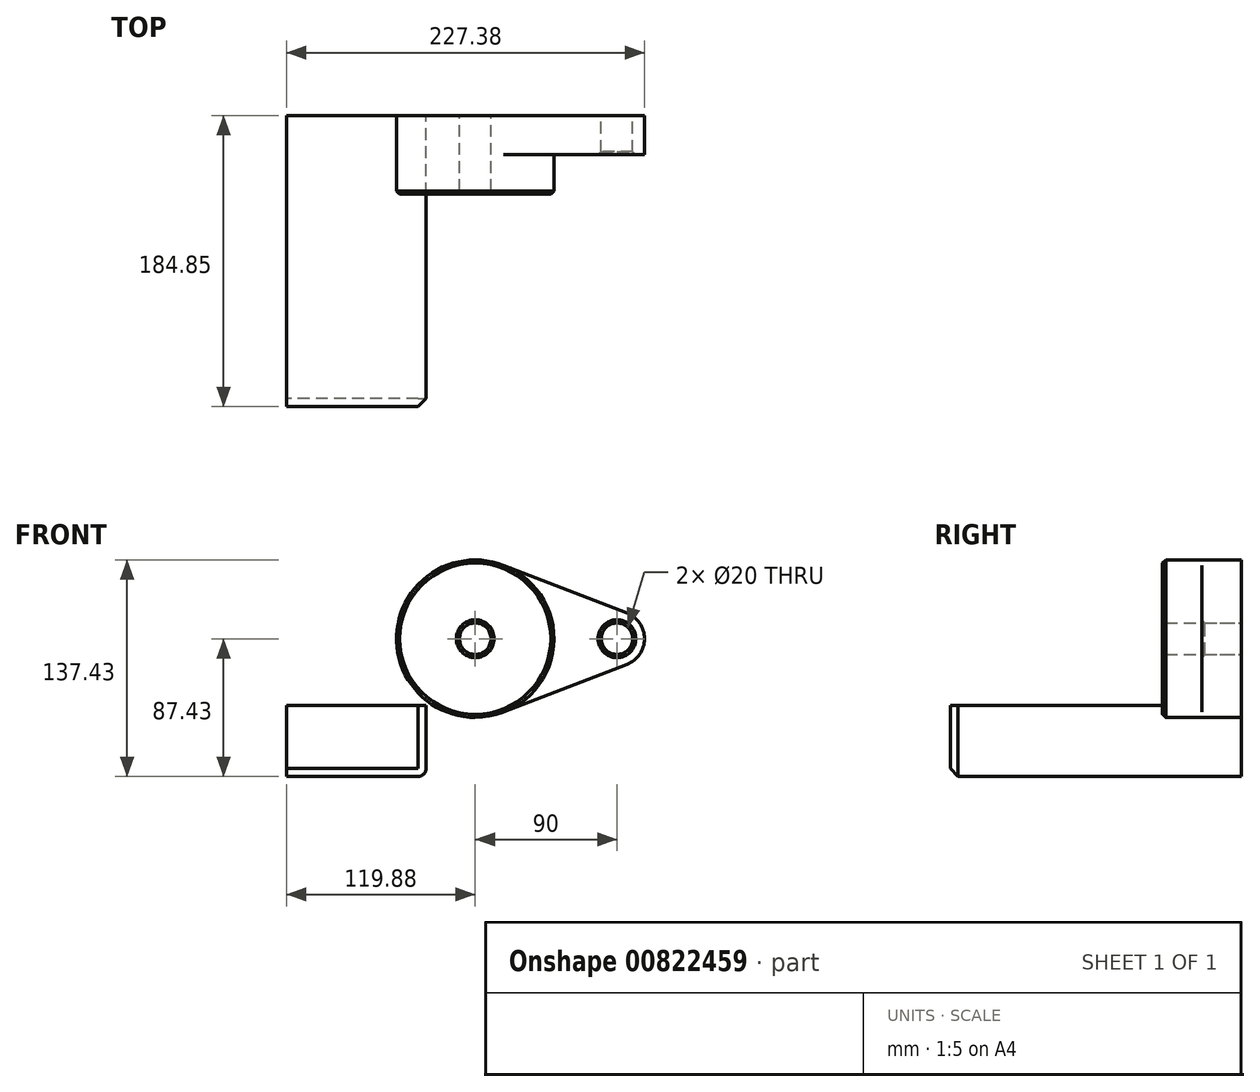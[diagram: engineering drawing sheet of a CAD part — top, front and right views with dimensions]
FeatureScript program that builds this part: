
annotation { "Feature Type Name" : "Feature", "Feature Type Description" : "" }
export const myFeature = defineFeature(function(context is Context, id is Id, definition is map)
    precondition{}
    {
        {
            var Q0;
            Q0=qCreatedBy(makeId("Front.planeOp"),FACE);
            var sketch = newSketch(context, id + "F0", { "sketchPlane" : qUnion([Q0])});
            skCircle(sketch, "E0", {"center": v(0, 0) * mm, "radius": 50 * mm});
            skCircle(sketch, "E1", {"center": v(90, 0) * mm, "radius": 17.5 * mm});
            skLineSegment(sketch, "E2", {"start": v(18.06, 46.63) * mm, "end": v(96.32, 16.32) * mm});
            skLineSegment(sketch, "E3", {"start": v(18.06, -46.63) * mm, "end": v(96.32, -16.32) * mm});
            skCircle(sketch, "E4", {"center": v(0, 0) * mm, "radius": 10 * mm});
            skCircle(sketch, "E5", {"center": v(90, 0) * mm, "radius": 10 * mm});
            skSolve(sketch);
        }
        {
            var Q0;
            Q0=qSketchRegion(id+"F0",true);
            extrude(context, id + "F1", {"entities" : qUnion([Q0]), "depth" : 25 * mm});
        }
        {
            var Q0;
            Q0=makeQuery(id+"F0.imprint","IMPRINT",FACE,{"disambiguationData":[TD([[makeQuery(id+"F0.imprint","IMPRINT",EDGE,{"derivedFrom":sQuery(id+"F0.wireOp",EDGE,"E4")}),-1.0]])]});
            extrude(context, id + "F2", {"entities" : qUnion([Q0]), "operationType" : NewBodyOperationType.ADD, "depth" : 50 * mm});
        }
        {
            var Q0;
            Q0=makeQuery(id+"F2.opExtrude","CAP_EDGE",EDGE,{"disambiguationData":[OSD([sQuery(id+"F0.wireOp",EDGE,"E0")])],"isStart":false});
            var Q1;
            Q1=makeQuery(id+"F2.opExtrude","CAP_EDGE",EDGE,{"disambiguationData":[OSD([sQuery(id+"F0.wireOp",EDGE,"E4")])],"isStart":false});
            var Q2;
            Q2=makeQuery(id+"F1.opExtrude","CAP_EDGE",EDGE,{"disambiguationData":[OSD([sQuery(id+"F0.wireOp",EDGE,"E5")])],"isStart":false});
            chamfer(context, id + "F3", {"entities" : qUnion([Q0, Q1, Q2]), "width" : 2 * mm, "tangentPropagation" : true});
        }
        {
            var Q0;
            Q0 = qSketchRegion(id + "F0", true);
            var sketch = newSketch(context, id + "F4", { "sketchPlane" : qUnion([Q0])});
            skLineSegment(sketch, "E6.bottom", {"start": v(-31.18, -87.43) * mm, "end": v(-119.88, -87.43) * mm});
            skLineSegment(sketch, "E6.top", {"start": v(-31.18, -42.53) * mm, "end": v(-119.88, -42.53) * mm});
            skLineSegment(sketch, "E6.left", {"start": v(-31.18, -87.43) * mm, "end": v(-31.18, -42.53) * mm});
            skLineSegment(sketch, "E6.right", {"start": v(-119.88, -87.43) * mm, "end": v(-119.88, -42.53) * mm});
            skSolve(sketch);
        }
        {
            var Q0;
            Q0 = qSketchRegion(id + "F4", true);
            extrude(context, id + "F5", {"entities" : qUnion([Q0]), "depth" : 184.85 * mm, "offsetDistance" : 25 * mm});
        }
        {
            var Q0;
            Q0=makeQuery(id+"F5.opExtrude","SWEPT_EDGE",EDGE,{"disambiguationData":[OSD([sQuery(id+"F4.wireOp",EDGE,"E6.bottom"),sQuery(id+"F4.wireOp",EDGE,"E6.left")])]});
            fillet(context, id + "F6", {"entities" : qUnion([Q0]), "radius" : 5 * mm, "tangentPropagation" : true, "allowEdgeOverflow" : false});
        }
        {
            var Q0;
            Q0=makeQuery(id+"F5.opExtrude","CAP_EDGE",EDGE,{"disambiguationData":[OSD([sQuery(id+"F4.wireOp",EDGE,"E6.bottom")])],"isStart":false});
            chamfer(context, id + "F7", {"entities" : qUnion([Q0]), "width" : 5 * mm, "tangentPropagation" : true});
        }
    });
